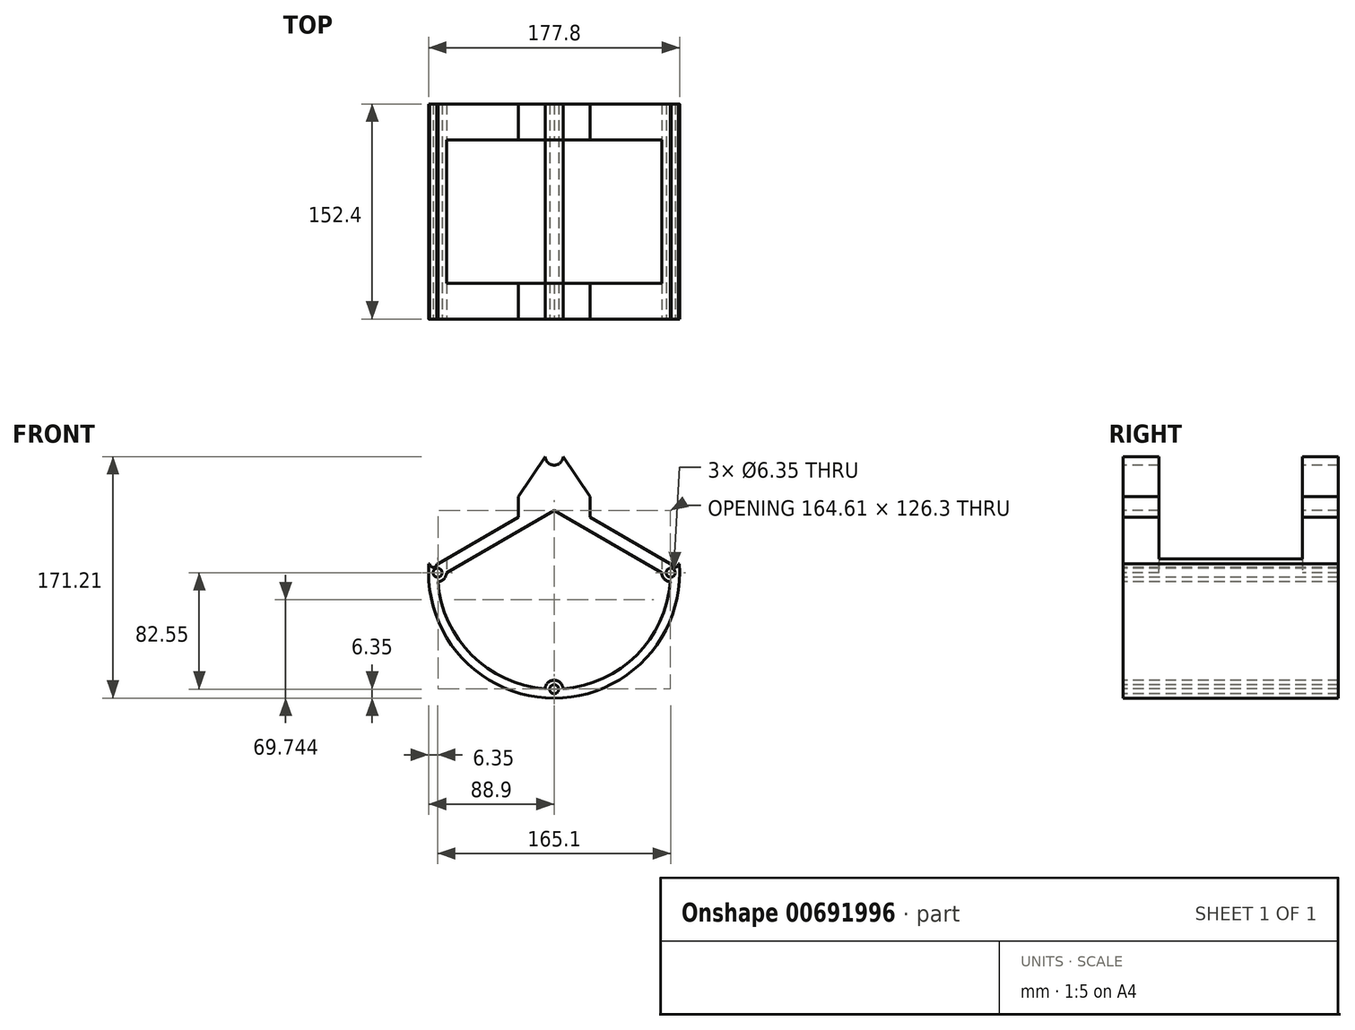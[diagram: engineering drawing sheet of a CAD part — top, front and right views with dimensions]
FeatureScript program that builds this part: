
annotation { "Feature Type Name" : "Feature", "Feature Type Description" : "" }
export const myFeature = defineFeature(function(context is Context, id is Id, definition is map)
    precondition{}
    {
        {
            var Q0;
            Q0=qCreatedBy(makeId("Front.planeOp"),FACE);
            var sketch = newSketch(context, id + "F0", { "sketchPlane" : qUnion([Q0])});
            skCircle(sketch, "E0", {"center": v(0, 0) * mm, "radius": 88.9 * mm});
            skLineSegment(sketch, "E1.bottom", {"start": v(88.9, 88.9) * mm, "end": v(-88.9, 88.9) * mm});
            skLineSegment(sketch, "E1.top", {"start": v(88.9, -88.9) * mm, "end": v(-88.9, -88.9) * mm});
            skLineSegment(sketch, "E1.left", {"start": v(88.9, 88.9) * mm, "end": v(88.9, -88.9) * mm});
            skLineSegment(sketch, "E1.right", {"start": v(-88.9, 88.9) * mm, "end": v(-88.9, -88.9) * mm});
            skLineSegment(sketch, "E2", {"start": v(-88.9, 88.9) * mm, "end": v(-38.1, 88.9) * mm});
            skLineSegment(sketch, "E3", {"start": v(-88.9, 88.9) * mm, "end": v(-88.9, 38.1) * mm});
            skLineSegment(sketch, "E4", {"start": v(-88.9, 38.1) * mm, "end": v(-38.1, 88.9) * mm});
            skLineSegment(sketch, "E5", {"start": v(-88.9, -88.9) * mm, "end": v(-38.1, -88.9) * mm});
            skLineSegment(sketch, "E6", {"start": v(-88.9, -88.9) * mm, "end": v(-88.9, -38.1) * mm});
            skLineSegment(sketch, "E7", {"start": v(-88.9, -38.1) * mm, "end": v(-38.1, -88.9) * mm});
            skLineSegment(sketch, "E8", {"start": v(88.9, 88.9) * mm, "end": v(88.9, 38.1) * mm});
            skLineSegment(sketch, "E9", {"start": v(88.9, 88.9) * mm, "end": v(38.1, 88.9) * mm});
            skLineSegment(sketch, "E10", {"start": v(38.1, 88.9) * mm, "end": v(88.9, 38.1) * mm});
            skLineSegment(sketch, "E11", {"start": v(88.9, -88.9) * mm, "end": v(88.9, -38.1) * mm});
            skLineSegment(sketch, "E12", {"start": v(88.9, -88.9) * mm, "end": v(38.1, -88.9) * mm});
            skLineSegment(sketch, "E13", {"start": v(38.1, -88.9) * mm, "end": v(88.9, -38.1) * mm});
            skSolve(sketch);
        }
        {
            var Q0;
            Q0=makeQuery(id+"F0.imprint","IMPRINT",FACE,{"disambiguationData":[TD([[makeQuery(id+"F0.imprint","IMPRINT",EDGE,{"derivedFrom":sQuery(id+"F0.wireOp",EDGE,"E0")}),1.0]])]});
            extrude(context, id + "F1", {"entities" : qUnion([Q0]), "oppositeDirection" : true, "depth" : 152.4 * mm, "offsetDistance" : 25.4 * mm});
        }
        {
            var Q0;
            Q0=makeQuery(id+"F0.imprint","IMPRINT",FACE,{"disambiguationData":[TD([[makeQuery(id+"F0.imprint","IMPRINT",EDGE,{"derivedFrom":sQuery(id+"F0.wireOp",EDGE,"E0")}),1.0]])]});
            var sketch = newSketch(context, id + "F2", { "sketchPlane" : qUnion([Q0])});
            skArc(sketch, "E14", {"start": v(-6.35, 82.3) * mm, "mid": v(0, 76.2) * mm, "end": v(6.35, 82.3) * mm});
            skCircle(sketch, "E15", {"center": v(82.55, 0) * mm, "radius": 6.35 * mm});
            skCircle(sketch, "E16", {"center": v(-82.55, 0) * mm, "radius": 6.35 * mm});
            skCircle(sketch, "E17", {"center": v(0, -82.55) * mm, "radius": 6.35 * mm});
            skArc(sketch, "E18.trimOffspring", {"start": v(6.35, -82.3) * mm, "mid": v(58.37, -58.37) * mm, "end": v(82.3, -6.35) * mm});
            skArc(sketch, "E19.trimOffspring", {"start": v(-82.3, -6.35) * mm, "mid": v(-58.37, -58.37) * mm, "end": v(-6.35, -82.3) * mm});
            skCircle(sketch, "E20", {"center": v(-82.55, 0) * mm, "radius": 3.18 * mm});
            skCircle(sketch, "E21", {"center": v(82.55, 0) * mm, "radius": 3.18 * mm});
            skCircle(sketch, "E22", {"center": v(0, -82.55) * mm, "radius": 3.18 * mm});
            skLineSegment(sketch, "E23", {"start": v(0, 0) * mm, "end": v(-76.2, 0) * mm});
            skLineSegment(sketch, "E24", {"start": v(-76.2, 0) * mm, "end": v(0, 44) * mm});
            skLineSegment(sketch, "E25", {"start": v(-82.3, 6.35) * mm, "end": v(-25.4, 39.2) * mm});
            skLineSegment(sketch, "E26", {"start": v(25.4, 39.2) * mm, "end": v(82.3, 6.35) * mm});
            skLineSegment(sketch, "E27", {"start": v(0, 44) * mm, "end": v(76.2, 0) * mm});
            skLineSegment(sketch, "E28", {"start": v(0, 53.86) * mm, "end": v(25.4, 53.86) * mm});
            skLineSegment(sketch, "E29", {"start": v(25.4, 53.86) * mm, "end": v(-25.4, 53.86) * mm});
            skLineSegment(sketch, "E30", {"start": v(-25.4, 53.86) * mm, "end": v(-25.4, 39.2) * mm});
            skLineSegment(sketch, "E31", {"start": v(25.4, 53.86) * mm, "end": v(25.4, 39.2) * mm});
            skLineSegment(sketch, "E32", {"start": v(6.35, 82.3) * mm, "end": v(25.4, 53.86) * mm});
            skLineSegment(sketch, "E33", {"start": v(-25.4, 53.86) * mm, "end": v(-6.35, 82.3) * mm});
            skSolve(sketch);
        }
        {
            var Q0;
            {var subQ0=sQuery(id+"F2.wireOp",EDGE,"pZnSbX1m-j3nH-xaNP-LMPN-0dnxHcCmeIX3");Q0=makeQuery(id+"F2.imprint","IMPRINT",FACE,{"disambiguationData":[TD([[makeQuery(id+"F2.imprint","IMPRINT",EDGE,{"derivedFrom":subQ0}),1.0]])]});}
            var Q1;
            Q1=makeQuery(id+"F2.imprint","IMPRINT",FACE,{"disambiguationData":[TD([[makeQuery(id+"F2.imprint","IMPRINT",EDGE,{"derivedFrom":sQuery(id+"F2.wireOp",EDGE,"E22")}),1.0]])]});
            var Q2;
            Q2=makeQuery(id+"F2.imprint","IMPRINT",FACE,{"disambiguationData":[TD([[makeQuery(id+"F2.imprint","IMPRINT",EDGE,{"derivedFrom":sQuery(id+"F2.wireOp",EDGE,"E21")}),1.0]])]});
            var Q3;
            Q3=makeQuery(id+"F2.imprint","IMPRINT",FACE,{"disambiguationData":[TD([[makeQuery(id+"F2.imprint","IMPRINT",EDGE,{"derivedFrom":sQuery(id+"F2.wireOp",EDGE,"PIKAohVv-ShRo-25By-NEcx-hEr0uxpBLTbm")}),1.0]])]});
            var Q4;
            Q4=makeQuery(id+"F2.imprint","IMPRINT",FACE,{"disambiguationData":[TD([[makeQuery(id+"F2.imprint","IMPRINT",EDGE,{"derivedFrom":sQuery(id+"F2.wireOp",EDGE,"E20")}),1.0]])]});
            extrude(context, id + "F3", {"entities" : qUnion([Q0, Q1, Q2, Q3, Q4]), "operationType" : NewBodyOperationType.REMOVE, "endBound" : BoundingType.THROUGH_ALL, "oppositeDirection" : true, "depth" : 25.4 * mm, "offsetDistance" : 25.4 * mm});
        }
        {
            var Q0;
            {var subQ0=sQuery(id+"F0.wireOp",EDGE,"E0");var subQ1=makeQuery(id+"F0.imprint","INTERSECT",VERTEX,{"derivedFrom":[subQ0,sQuery(id+"F0.wireOp",EDGE,"E1.left")]});Q0=makeQuery(id+"F0.imprint","IMPRINT",FACE,{"disambiguationData":[TD([[makeQuery(id+"F0.imprint","IMPRINT",EDGE,{"disambiguationData":[TD([[subQ1,1.0]])],"derivedFrom":subQ0}),1.0]])]});}
            var sketch = newSketch(context, id + "F4", { "sketchPlane" : qUnion([Q0])});
            skLineSegment(sketch, "E34", {"start": v(0, 0) * mm, "end": v(-88.85, 0) * mm});
            skLineSegment(sketch, "E35", {"start": v(0, 0) * mm, "end": v(0, 6.35) * mm});
            skLineSegment(sketch, "E36", {"start": v(0, 6.35) * mm, "end": v(-94.2, 6.35) * mm});
            skLineSegment(sketch, "E37", {"start": v(-94.2, 6.35) * mm, "end": v(-94.2, 107.1) * mm});
            skLineSegment(sketch, "E38", {"start": v(-94.2, 107.1) * mm, "end": v(114.28, 107.1) * mm});
            skLineSegment(sketch, "E39", {"start": v(0, 6.35) * mm, "end": v(132.6, 6.35) * mm});
            skLineSegment(sketch, "E40", {"start": v(132.6, 6.35) * mm, "end": v(114.28, 107.1) * mm});
            skSolve(sketch);
        }
        {
            var Q0;
            Q0 = qSketchRegion(id + "F4", true);
            extrude(context, id + "F5", {"entities" : qUnion([Q0]), "operationType" : NewBodyOperationType.REMOVE, "endBound" : BoundingType.THROUGH_ALL, "oppositeDirection" : true, "depth" : 25.4 * mm, "offsetDistance" : 25.4 * mm});
        }
        {
            var Q0;
            {var subQ0=sQuery(id+"F0.wireOp",EDGE,"E0");var subQ1=makeQuery(id+"F0.imprint","INTERSECT",VERTEX,{"derivedFrom":[subQ0,sQuery(id+"F0.wireOp",EDGE,"E1.left")]});Q0=makeQuery(id+"F0.imprint","IMPRINT",FACE,{"disambiguationData":[TD([[makeQuery(id+"F0.imprint","IMPRINT",EDGE,{"disambiguationData":[TD([[subQ1,1.0]])],"derivedFrom":subQ0}),1.0]])]});}
            var sketch = newSketch(context, id + "F6", { "sketchPlane" : qUnion([Q0])});
            skLineSegment(sketch, "E41", {"start": v(0, 0) * mm, "end": v(-82.55, 0) * mm});
            skLineSegment(sketch, "E42", {"start": v(-82.55, 0) * mm, "end": v(-82.55, 6.35) * mm});
            skLineSegment(sketch, "E43", {"start": v(-82.55, 6.35) * mm, "end": v(-85.6, 6.35) * mm});
            skCircle(sketch, "E44", {"center": v(-85.6, 6.35) * mm, "radius": 2.54 * mm});
            skLineSegment(sketch, "E45", {"start": v(0, 0) * mm, "end": v(82.55, 0) * mm});
            skLineSegment(sketch, "E46", {"start": v(82.55, 0) * mm, "end": v(82.55, 6.35) * mm});
            skLineSegment(sketch, "E47", {"start": v(82.55, 6.35) * mm, "end": v(85.6, 6.35) * mm});
            skCircle(sketch, "E48", {"center": v(85.6, 6.35) * mm, "radius": 2.54 * mm});
            skSolve(sketch);
        }
        {
            var Q0;
            Q0 = qSketchRegion(id + "F6", true);
            var Q1;
            {var subQ0=sQuery(id+"F2.wireOp",EDGE,"E18.trimOffspring");Q1=makeQuery(id+"F2.imprint","IMPRINT",FACE,{"disambiguationData":[TD([[makeQuery(id+"F2.imprint","IMPRINT",EDGE,{"derivedFrom":subQ0}),1.0]])]});}
            extrude(context, id + "F7", {"entities" : qUnion([Q0, Q1]), "operationType" : NewBodyOperationType.REMOVE, "endBound" : BoundingType.THROUGH_ALL, "oppositeDirection" : true, "depth" : 25.4 * mm, "offsetDistance" : 25.4 * mm});
        }
        {
            var Q0;
            {var subQ1=sQuery(id+"F2.wireOp",EDGE,"E24");Q0=makeQuery(id+"F2.imprint","IMPRINT",FACE,{"disambiguationData":[TD([[makeQuery(id+"F2.imprint","IMPRINT",EDGE,{"derivedFrom":subQ1}),1.0]])]});}
            var Q1;
            Q1=makeQuery(id+"F2.imprint","IMPRINT",FACE,{"disambiguationData":[TD([[makeQuery(id+"F2.imprint","IMPRINT",EDGE,{"derivedFrom":sQuery(id+"F2.wireOp",EDGE,"E14")}),-1.0]])]});
            extrude(context, id + "F8", {"entities" : qUnion([Q0, Q1]), "operationType" : NewBodyOperationType.ADD, "oppositeDirection" : true, "depth" : 152.4 * mm, "offsetDistance" : 25.4 * mm});
        }
        {
            var Q0;
            Q0=qCreatedBy(makeId("Top.planeOp"),FACE);
            var sketch = newSketch(context, id + "F9", { "sketchPlane" : qUnion([Q0])});
            skLineSegment(sketch, "E49.bottom", {"start": v(76.2, 152.4) * mm, "end": v(-76.2, 152.4) * mm});
            skLineSegment(sketch, "E49.top", {"start": v(76.2, -152.4) * mm, "end": v(-76.2, -152.4) * mm});
            skLineSegment(sketch, "E49.left", {"start": v(76.2, 152.4) * mm, "end": v(76.2, -152.4) * mm});
            skLineSegment(sketch, "E49.right", {"start": v(-76.2, 152.4) * mm, "end": v(-76.2, -152.4) * mm});
            skPoint(sketch, "E49.middle", {"position": v(0, 0) * mm});
            skLineSegment(sketch, "E50", {"start": v(-76.2, 0) * mm, "end": v(-76.2, 25.4) * mm});
            skLineSegment(sketch, "E51", {"start": v(-76.2, 25.4) * mm, "end": v(76.2, 25.4) * mm});
            skLineSegment(sketch, "E52", {"start": v(76.2, 25.4) * mm, "end": v(76.2, 127) * mm});
            skLineSegment(sketch, "E53", {"start": v(76.2, 127) * mm, "end": v(-76.2, 127) * mm});
            skSolve(sketch);
        }
        {
            var Q0;
            {var subQ0=sQuery(id+"F9.wireOp",EDGE,"E51");Q0=makeQuery(id+"F9.imprint","IMPRINT",FACE,{"disambiguationData":[TD([[makeQuery(id+"F9.imprint","IMPRINT",EDGE,{"derivedFrom":subQ0}),1.0]])]});}
            extrude(context, id + "F10", {"entities" : qUnion([Q0]), "operationType" : NewBodyOperationType.REMOVE, "endBound" : BoundingType.THROUGH_ALL, "depth" : 25.4 * mm, "offsetDistance" : 25.4 * mm});
        }
    });
